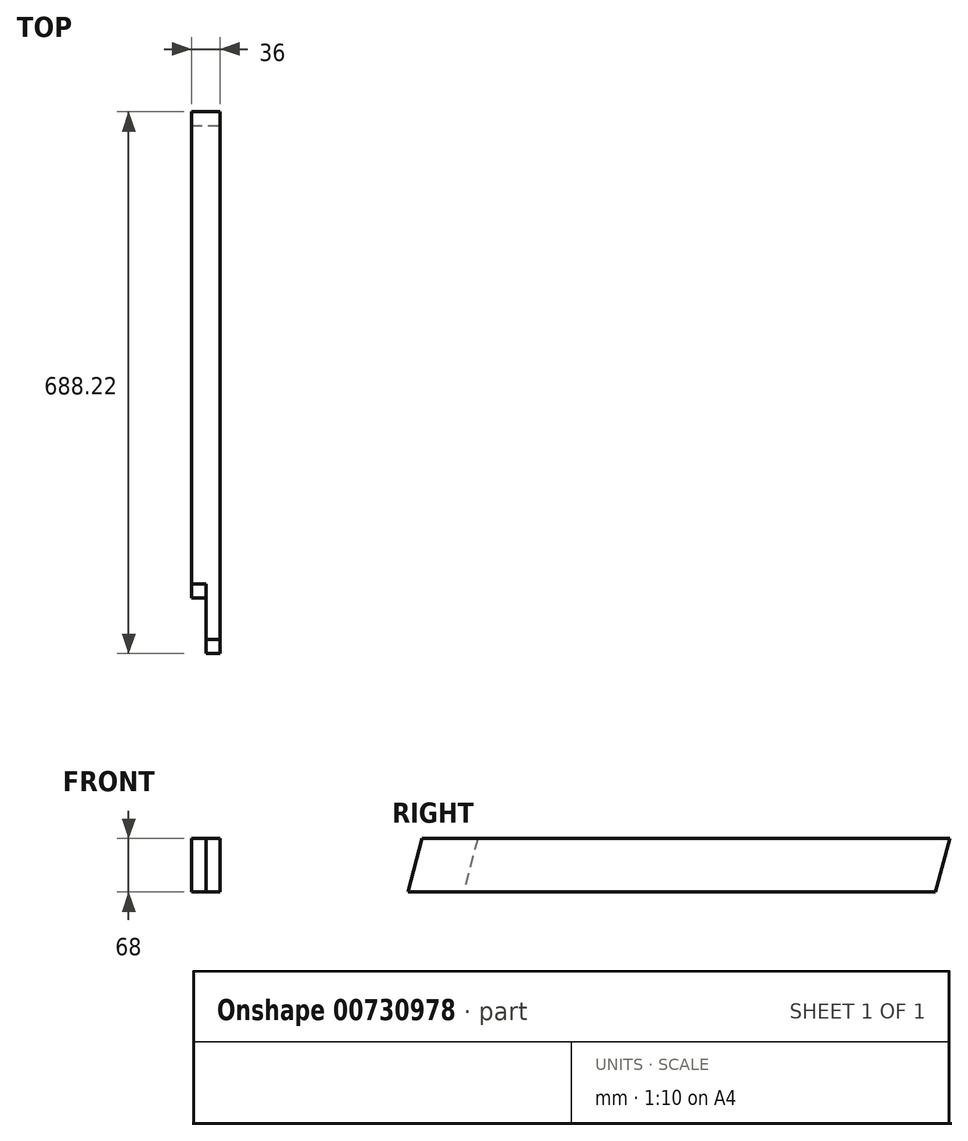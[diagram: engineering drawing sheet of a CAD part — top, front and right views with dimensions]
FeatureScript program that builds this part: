
annotation { "Feature Type Name" : "Feature", "Feature Type Description" : "" }
export const myFeature = defineFeature(function(context is Context, id is Id, definition is map)
    precondition{}
    {
        {
            var Q0;
            Q0=qCreatedBy(makeId("Front.planeOp"),FACE);
            var sketch = newSketch(context, id + "F0", { "sketchPlane" : qUnion([Q0])});
            skLineSegment(sketch, "E0.bottom", {"start": v(18, -34) * mm, "end": v(-18, -34) * mm});
            skLineSegment(sketch, "E0.top", {"start": v(18, 34) * mm, "end": v(-18, 34) * mm});
            skLineSegment(sketch, "E0.left", {"start": v(18, -34) * mm, "end": v(18, 34) * mm});
            skLineSegment(sketch, "E0.right", {"start": v(-18, -34) * mm, "end": v(-18, 34) * mm});
            skPoint(sketch, "E0.middle", {"position": v(0, 0) * mm});
            skSolve(sketch);
        }
        {
            var Q0;
            Q0=makeQuery(id+"F0.imprint","IMPRINT",FACE,{"disambiguationData":[TD([[makeQuery(id+"F0.imprint","IMPRINT",EDGE,{"derivedFrom":sQuery(id+"F0.wireOp",EDGE,"E0.bottom")}),-1.0]])]});
            extrude(context, id + "F1", {"entities" : qUnion([Q0]), "depth" : 750 * mm, "offsetDistance" : 25 * mm});
        }
        {
            var Q0;
            Q0=makeQuery(id+"F1.opExtrude","SWEPT_FACE",FACE,{"disambiguationData":[OSD([sQuery(id+"F0.wireOp",EDGE,"E0.right")])]});
            var sketch = newSketch(context, id + "F2", { "sketchPlane" : qUnion([Q0])});
            skLineSegment(sketch, "E1", {"start": v(0, 34) * mm, "end": v(18.22, -34) * mm});
            skLineSegment(sketch, "E2", {"start": v(18.22, -34) * mm, "end": v(0, -34) * mm});
            skLineSegment(sketch, "E3", {"start": v(0, -34) * mm, "end": v(0, 34) * mm});
            skLineSegment(sketch, "E4", {"start": v(688.22, -34) * mm, "end": v(670, 34) * mm});
            skLineSegment(sketch, "E5", {"start": v(670, 34) * mm, "end": v(750, 34) * mm});
            skLineSegment(sketch, "E6", {"start": v(750, 34) * mm, "end": v(750, -34) * mm});
            skLineSegment(sketch, "E7", {"start": v(750, -34) * mm, "end": v(688.22, -34) * mm});
            skSolve(sketch);
        }
        {
            var Q0;
            Q0=makeQuery(id+"F2.imprint","IMPRINT",FACE,{"disambiguationData":[TD([[makeQuery(id+"F2.imprint","IMPRINT",EDGE,{"derivedFrom":sQuery(id+"F2.wireOp",EDGE,"E1")}),-1.0]])]});
            var Q1;
            Q1=makeQuery(id+"F2.imprint","IMPRINT",FACE,{"disambiguationData":[TD([[makeQuery(id+"F2.imprint","IMPRINT",EDGE,{"derivedFrom":sQuery(id+"F2.wireOp",EDGE,"E4")}),-1.0]])]});
            extrude(context, id + "F3", {"entities" : qUnion([Q0, Q1]), "operationType" : NewBodyOperationType.REMOVE, "endBound" : BoundingType.UP_TO_NEXT, "oppositeDirection" : true, "depth" : 25 * mm, "offsetDistance" : 25 * mm});
        }
        {
            var Q0;
            Q0=makeQuery(id+"F1.opExtrude","SWEPT_FACE",FACE,{"disambiguationData":[OSD([sQuery(id+"F0.wireOp",EDGE,"E0.right")])]});
            var sketch = newSketch(context, id + "F4", { "sketchPlane" : qUnion([Q0])});
            skLineSegment(sketch, "E8", {"start": v(599.5, 34) * mm, "end": v(670, 34) * mm});
            skLineSegment(sketch, "E9", {"start": v(599.5, 34) * mm, "end": v(617.72, -34) * mm});
            skLineSegment(sketch, "E10", {"start": v(688.22, -34) * mm, "end": v(617.72, -34) * mm});
            skLineSegment(sketch, "E11", {"start": v(688.22, -34) * mm, "end": v(670, 34) * mm});
            skSolve(sketch);
        }
        {
            var Q0;
            Q0=makeQuery(id+"F4.imprint","IMPRINT",FACE,{"disambiguationData":[TD([[makeQuery(id+"F4.imprint","IMPRINT",EDGE,{"derivedFrom":sQuery(id+"F4.wireOp",EDGE,"E8")}),1.0]])]});
            extrude(context, id + "F5", {"entities" : qUnion([Q0]), "operationType" : NewBodyOperationType.REMOVE, "oppositeDirection" : true, "depth" : 18 * mm, "offsetDistance" : 25 * mm});
        }
    });
